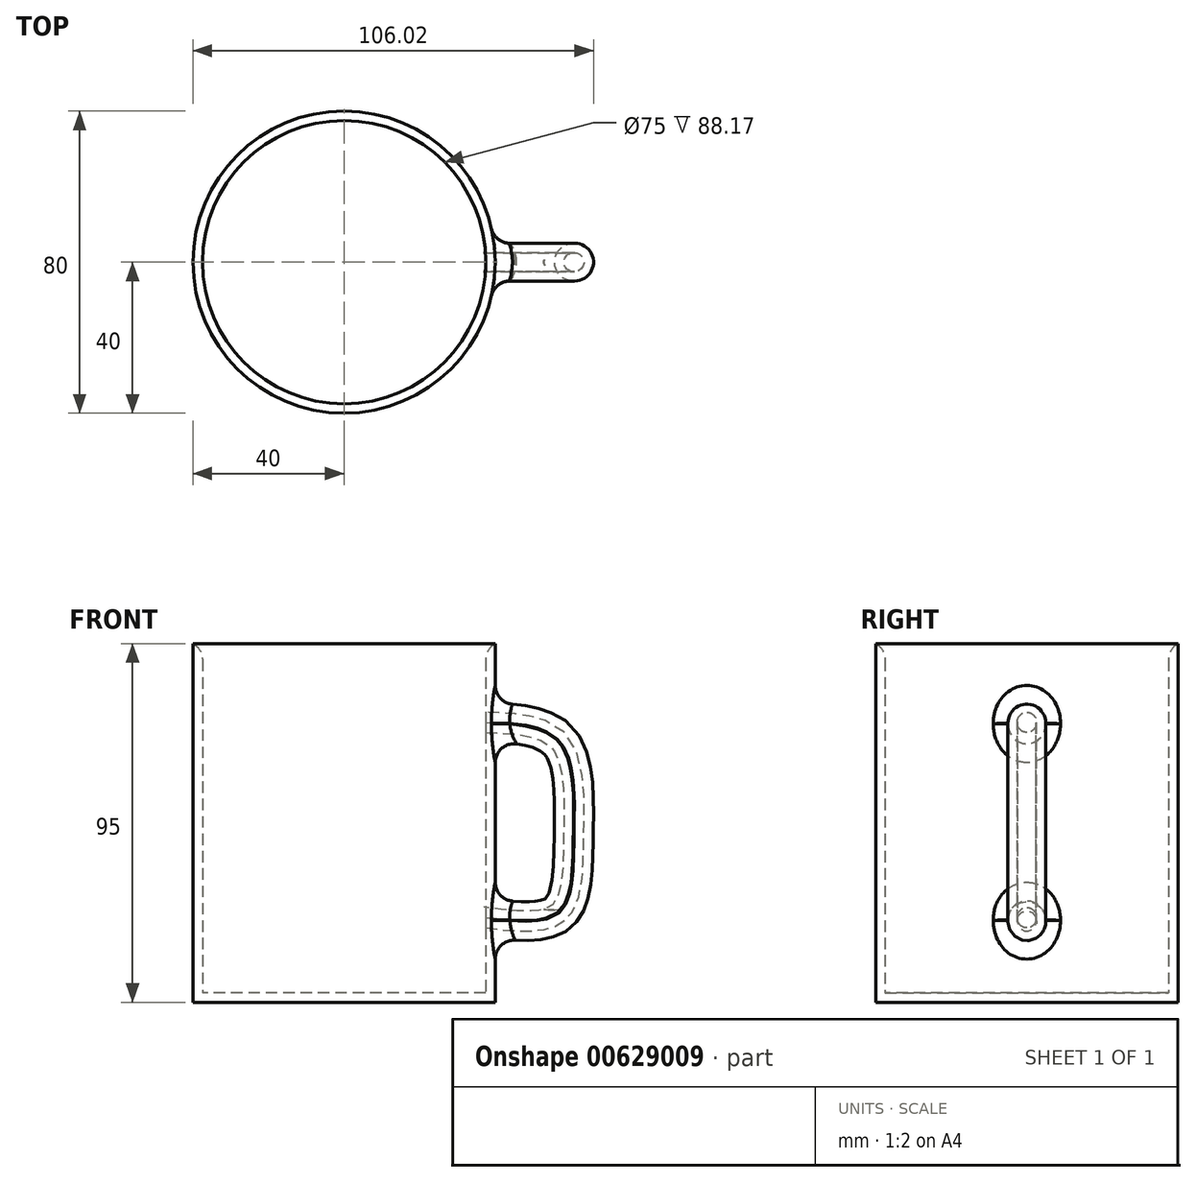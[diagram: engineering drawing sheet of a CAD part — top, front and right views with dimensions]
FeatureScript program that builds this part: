
annotation { "Feature Type Name" : "Feature", "Feature Type Description" : "" }
export const myFeature = defineFeature(function(context is Context, id is Id, definition is map)
    precondition{}
    {
        {
            var Q0;
            Q0=qCreatedBy(makeId("Top.planeOp"),FACE);
            var sketch = newSketch(context, id + "F0", { "sketchPlane" : qUnion([Q0])});
            skCircle(sketch, "E0", {"center": v(0, 0) * mm, "radius": 40 * mm});
            skSolve(sketch);
        }
        {
            var Q0;
            Q0=qSketchRegion(id+"F0",true);
            extrude(context, id + "F1", {"entities" : qUnion([Q0]), "depth" : 95 * mm, "offsetDistance" : 25 * mm});
        }
        {
            var Q0;
            Q0=qCreatedBy(makeId("Front.planeOp"),FACE);
            var sketch = newSketch(context, id + "F2", { "sketchPlane" : qUnion([Q0])});
            skFitSpline(sketch, "E1", {"points": [v(35.08, 74.87) * mm, v(57.4, 69.5) * mm, v(61.43, 43.68) * mm, v(57.13, 23.25) * mm, v(34.28, 22.18) * mm], "startDerivative": vector(107.98, -2.54) * mm, "endDerivative": vector(-111.14, 15.84) * mm});
            skSolve(sketch);
        }
        {
            var Q0;
            Q0=qCreatedBy(makeId("Right.planeOp"),FACE);
            cPlane(context, id + "F3", {"entities" : qUnion([Q0]), "cplaneType" : CPlaneType.OFFSET, "offset" : 34.1 * mm, "width" : 150 * mm, "height" : 150 * mm});
        }
        {
            var Q0;
            Q0=qCreatedBy(id+"F3.planeOp",FACE);
            var sketch = newSketch(context, id + "F4", { "sketchPlane" : qUnion([Q0])});
            skCircle(sketch, "E2", {"center": v(0, 74.38) * mm, "radius": 5 * mm});
            skSolve(sketch);
        }
        {
            var Q0;
            Q0=qCreatedBy(id+"F3.planeOp",FACE);
            var sketch = newSketch(context, id + "F5", { "sketchPlane" : qUnion([Q0])});
            skCircle(sketch, "E3", {"center": v(0, 23.1) * mm, "radius": 5 * mm});
            skSolve(sketch);
        }
        {
            var Q0;
            Q0=qSketchRegion(id+"F4",true);
            var Q1;
            Q1=qSketchRegion(id+"F5",true);
            var Q2;
            Q2=qConstructionFilter(qBodyType(qCreatedBy(id+"F2",EDGE),BodyType.WIRE),ConstructionObject.NO);
            sweep(context, id + "F6", {"operationType" : NewBodyOperationType.ADD, "profiles" : qUnion([Q0, Q1]), "path" : qUnion([Q2])});
        }
        {
            var Q0;
            Q0=makeQuery(id+"F1.opExtrude","CAP_FACE",FACE,{"disambiguationData":[OSD([sQuery(id+"F0.wireOp",EDGE,"E0")])],"isStart":false});
            shell(context, id + "F7", {"entities" : qUnion([Q0]), "thickness" : 2.5 * mm});
        }
        {
            var Q0;
            Q0=makeQuery(id+"F6.opSweep","SWEPT_FACE",FACE,{"disambiguationData":[OSD([sQuery(id+"F2.wireOp",EDGE,"E1"),sQuery(id+"F4.wireOp",EDGE,"E2")])]});
            var Q1;
            Q1=makeQuery(id+"F6.opSweep","SWEPT_FACE",FACE,{"disambiguationData":[OSD([sQuery(id+"F2.wireOp",EDGE,"E1"),sQuery(id+"F5.wireOp",EDGE,"E3")])]});
            fillet(context, id + "F8", {"entities" : qUnion([Q0, Q1]), "radius" : 5 * mm, "tangentPropagation" : true, "allowEdgeOverflow" : false});
        }
        {
            var Q0;
            {var subQ0=sQuery(id+"F0.wireOp",EDGE,"E0");Q0=makeQuery(id+"F7.opShell","OFFSET_EDGE",EDGE,{"disambiguationData":[OSD([subQ0]),TDD([makeQuery(id+"F1.opExtrude","CAP_EDGE",EDGE,{"disambiguationData":[OSD([subQ0])],"isStart":false})])]});}
            fillet(context, id + "F9", {"entities" : qUnion([Q0]), "radius" : 5 * mm, "tangentPropagation" : true, "allowEdgeOverflow" : false});
        }
    });
